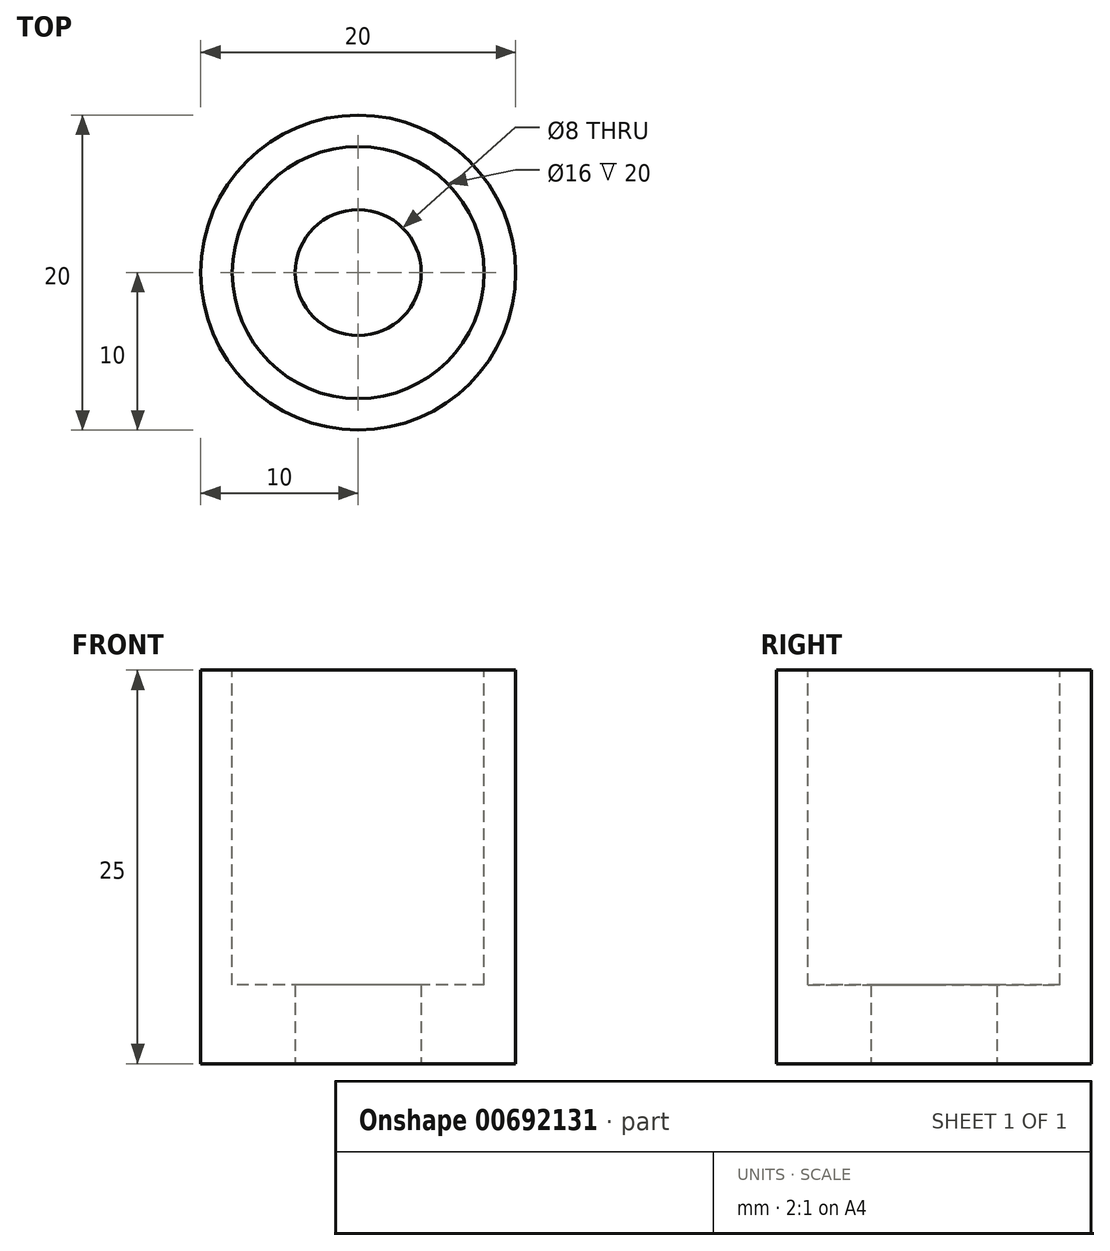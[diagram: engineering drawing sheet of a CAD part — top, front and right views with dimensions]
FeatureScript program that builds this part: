
annotation { "Feature Type Name" : "Feature", "Feature Type Description" : "" }
export const myFeature = defineFeature(function(context is Context, id is Id, definition is map)
    precondition{}
    {
        {
            var Q0;
            Q0=qCreatedBy(makeId("Top.planeOp"),FACE);
            var sketch = newSketch(context, id + "F0", { "sketchPlane" : qUnion([Q0])});
            skCircle(sketch, "E0", {"center": v(0, 0) * mm, "radius": 10 * mm});
            skCircle(sketch, "E1", {"center": v(0, 0) * mm, "radius": 4 * mm});
            skSolve(sketch);
        }
        {
            var Q0;
            Q0 = qSketchRegion(id + "F0", true);
            extrude(context, id + "F1", {"entities" : qUnion([Q0]), "depth" : 25 * mm, "offsetDistance" : 25 * mm});
        }
        {
            var Q0;
            Q0=makeQuery(id+"F1.opExtrude","CAP_FACE",FACE,{"disambiguationData":[OSD([sQuery(id+"F0.wireOp",EDGE,"E0")])],"isStart":false});
            var sketch = newSketch(context, id + "F2", { "sketchPlane" : qUnion([Q0])});
            skCircle(sketch, "E2", {"center": v(0, 0) * mm, "radius": 8 * mm});
            skSolve(sketch);
        }
        {
            var Q0;
            Q0 = qSketchRegion(id + "F2", true);
            extrude(context, id + "F3", {"entities" : qUnion([Q0]), "operationType" : NewBodyOperationType.REMOVE, "oppositeDirection" : true, "depth" : 20 * mm, "offsetDistance" : 25 * mm});
        }
        {
            var Q0;
            Q0 = qSketchRegion(id + "F0", true);
            extrude(context, id + "F4", {"entities" : qUnion([Q0]), "operationType" : NewBodyOperationType.ADD, "depth" : 5 * mm, "offsetDistance" : 25 * mm});
        }
    });
